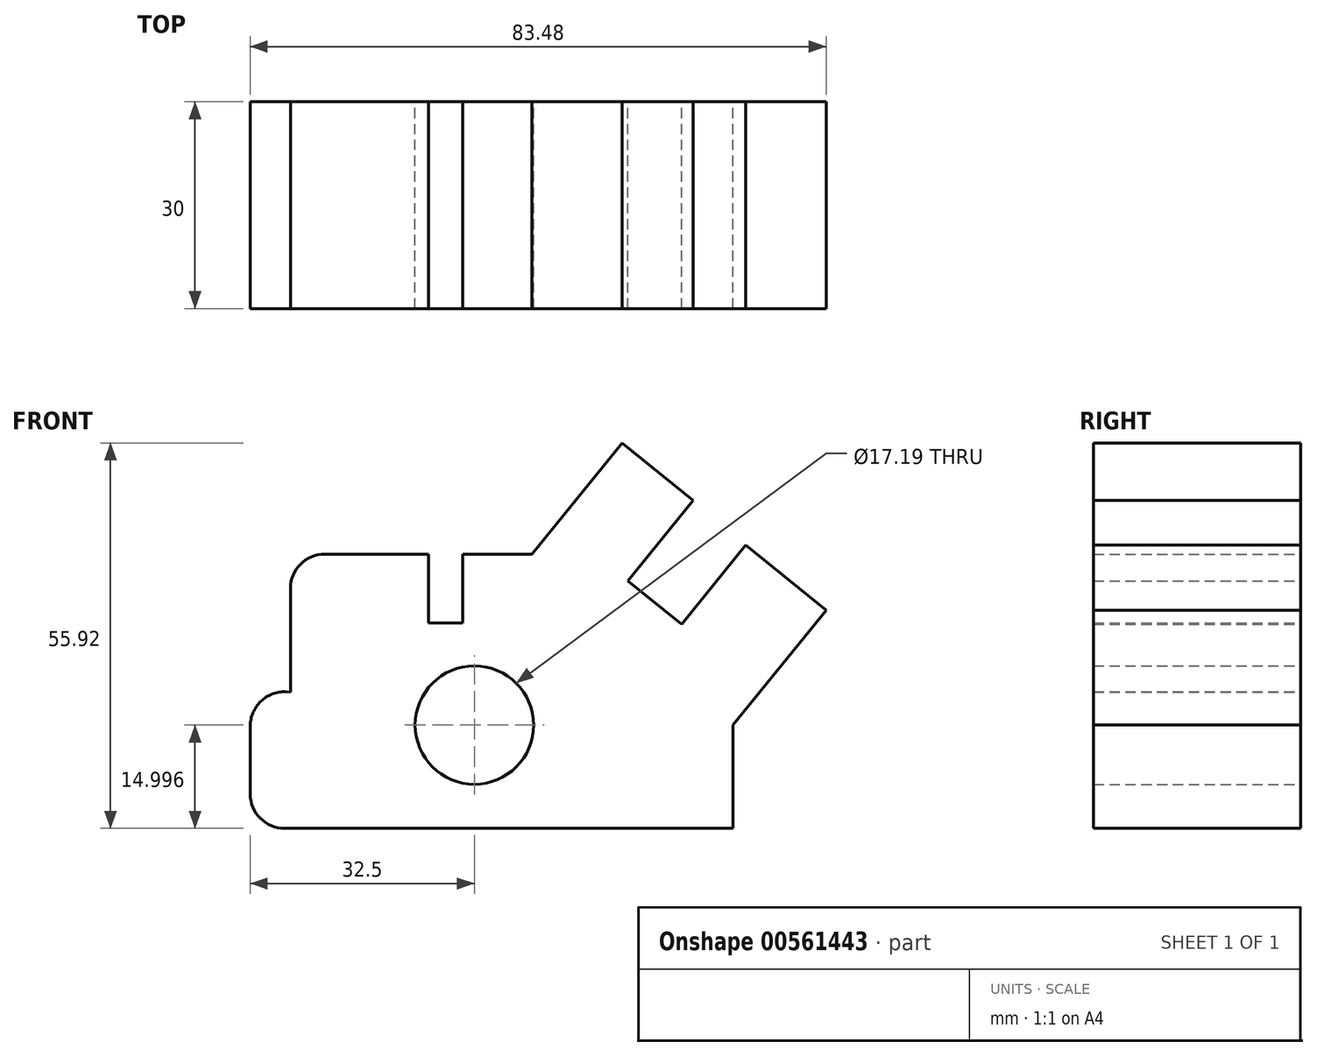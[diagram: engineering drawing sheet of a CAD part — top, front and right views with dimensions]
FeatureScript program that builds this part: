
annotation { "Feature Type Name" : "Feature", "Feature Type Description" : "" }
export const myFeature = defineFeature(function(context is Context, id is Id, definition is map)
    precondition{}
    {
        {
            var Q0;
            Q0=qCreatedBy(makeId("Front.planeOp"),FACE);
            var sketch = newSketch(context, id + "F0", { "sketchPlane" : qUnion([Q0])});
            skLineSegment(sketch, "E0.top", {"start": v(-27.5, -30.23) * mm, "end": v(37.5, -30.23) * mm});
            skLineSegment(sketch, "E0.left", {"start": v(-32.5, -15.4) * mm, "end": v(-32.5, -25.23) * mm});
            skLineSegment(sketch, "E0.right", {"start": v(37.5, -15.23) * mm, "end": v(37.5, -30.23) * mm});
            skLineSegment(sketch, "E1", {"start": v(37.5, -15.23) * mm, "end": v(50.98, 1.4) * mm});
            skLineSegment(sketch, "E2", {"start": v(50.98, 1.4) * mm, "end": v(39.32, 10.85) * mm});
            skLineSegment(sketch, "E3", {"start": v(39.32, 10.85) * mm, "end": v(30.03, -0.62) * mm});
            skLineSegment(sketch, "E4", {"start": v(30.03, -0.62) * mm, "end": v(22.26, 5.68) * mm});
            skLineSegment(sketch, "E5", {"start": v(22.26, 5.68) * mm, "end": v(31.7, 17.34) * mm});
            skLineSegment(sketch, "E6", {"start": v(31.7, 17.34) * mm, "end": v(21.39, 25.7) * mm});
            skLineSegment(sketch, "E7", {"start": v(21.39, 25.7) * mm, "end": v(8.33, 9.57) * mm});
            skLineSegment(sketch, "E8", {"start": v(8.33, 9.57) * mm, "end": v(-1.67, 9.57) * mm});
            skLineSegment(sketch, "E9", {"start": v(-1.67, 9.57) * mm, "end": v(-1.67, -0.43) * mm});
            skLineSegment(sketch, "E10", {"start": v(-1.67, -0.43) * mm, "end": v(-6.67, -0.43) * mm});
            skLineSegment(sketch, "E11", {"start": v(-6.67, -0.43) * mm, "end": v(-6.67, 9.57) * mm});
            skLineSegment(sketch, "E12", {"start": v(-6.67, 9.57) * mm, "end": v(-21.67, 9.57) * mm});
            skLineSegment(sketch, "E13", {"start": v(-26.67, 4.57) * mm, "end": v(-26.67, -10.43) * mm});
            skLineSegment(sketch, "E14", {"start": v(-26.67, -10.43) * mm, "end": v(-27.33, -10.4) * mm});
            skCircle(sketch, "E15", {"center": v(0, -15.23) * mm, "radius": 8.6 * mm});
            skPoint(sketch, "E16.visualSharp", {"position": v(-32.5, -10.23) * mm});
            skArc(sketch, "E16.filletArc", {"start": v(-27.33, -10.4) * mm, "mid": v(-30.98, -11.81) * mm, "end": v(-32.5, -15.4) * mm});
            skPoint(sketch, "E17.visualSharp", {"position": v(-32.5, -30.23) * mm});
            skArc(sketch, "E17.filletArc", {"start": v(-32.5, -25.23) * mm, "mid": v(-31.04, -28.77) * mm, "end": v(-27.5, -30.23) * mm});
            skPoint(sketch, "E18.visualSharp", {"position": v(-26.67, 9.57) * mm});
            skArc(sketch, "E18.filletArc", {"start": v(-21.67, 9.57) * mm, "mid": v(-25.2, 8.1) * mm, "end": v(-26.67, 4.57) * mm});
            skSolve(sketch);
        }
        {
            var Q0;
            Q0 = qSketchRegion(id + "F0", true);
            extrude(context, id + "F1", {"entities" : qUnion([Q0]), "depth" : 30 * mm, "offsetDistance" : 25 * mm});
        }
    });
